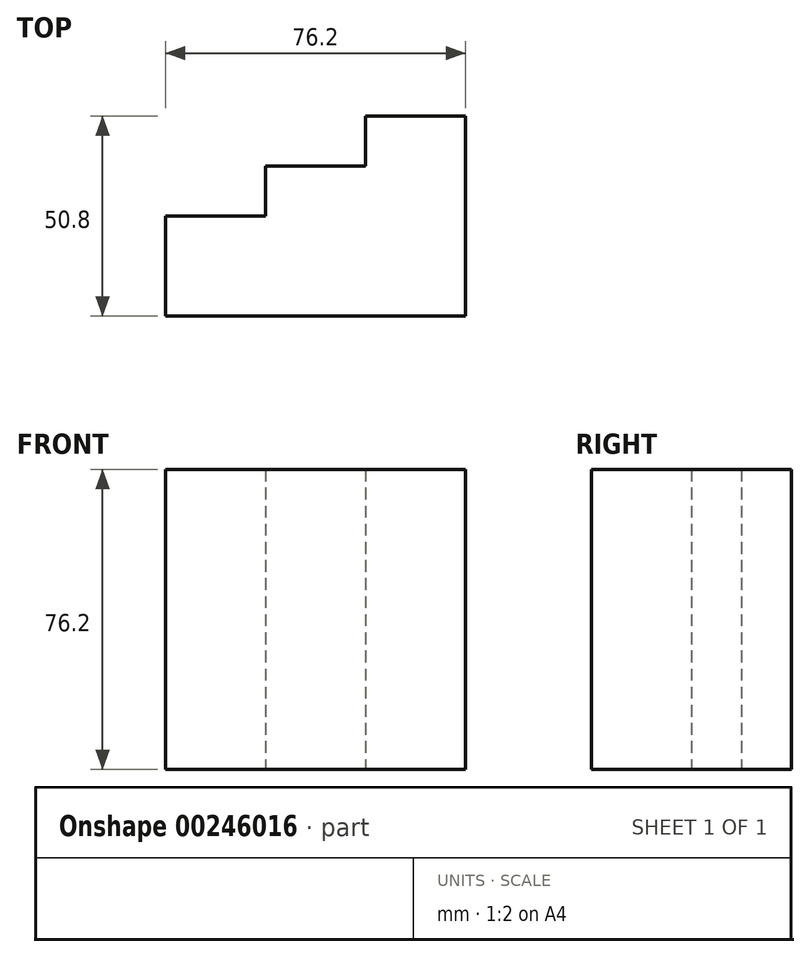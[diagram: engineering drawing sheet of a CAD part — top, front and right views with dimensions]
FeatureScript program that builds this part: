
annotation { "Feature Type Name" : "Feature", "Feature Type Description" : "" }
export const myFeature = defineFeature(function(context is Context, id is Id, definition is map)
    precondition{}
    {
        {
            var Q0;
            Q0=qCreatedBy(makeId("Top.planeOp"),FACE);
            var sketch = newSketch(context, id + "F0", { "sketchPlane" : qUnion([Q0])});
            skLineSegment(sketch, "E0", {"start": v(0, 0) * mm, "end": v(76.2, 0) * mm});
            skLineSegment(sketch, "E1", {"start": v(76.2, 0) * mm, "end": v(76.2, 50.8) * mm});
            skLineSegment(sketch, "E2", {"start": v(76.2, 50.8) * mm, "end": v(50.8, 50.8) * mm});
            skLineSegment(sketch, "E3", {"start": v(50.8, 50.8) * mm, "end": v(50.8, 38.1) * mm});
            skLineSegment(sketch, "E4", {"start": v(50.8, 38.1) * mm, "end": v(25.4, 38.1) * mm});
            skLineSegment(sketch, "E5", {"start": v(25.4, 38.1) * mm, "end": v(25.4, 25.4) * mm});
            skLineSegment(sketch, "E6", {"start": v(25.4, 25.4) * mm, "end": v(0, 25.4) * mm});
            skLineSegment(sketch, "E7", {"start": v(0, 25.4) * mm, "end": v(0, 0) * mm});
            skSolve(sketch);
        }
        {
            var Q0;
            Q0=makeQuery(id+"F0.imprint","IMPRINT",FACE,{"disambiguationData":[TD([[makeQuery(id+"F0.imprint","IMPRINT",EDGE,{"derivedFrom":sQuery(id+"F0.wireOp",EDGE,"E0")}),1.0]])]});
            extrude(context, id + "F1", {"entities" : qUnion([Q0]), "depth" : 76.2 * mm});
        }
    });
